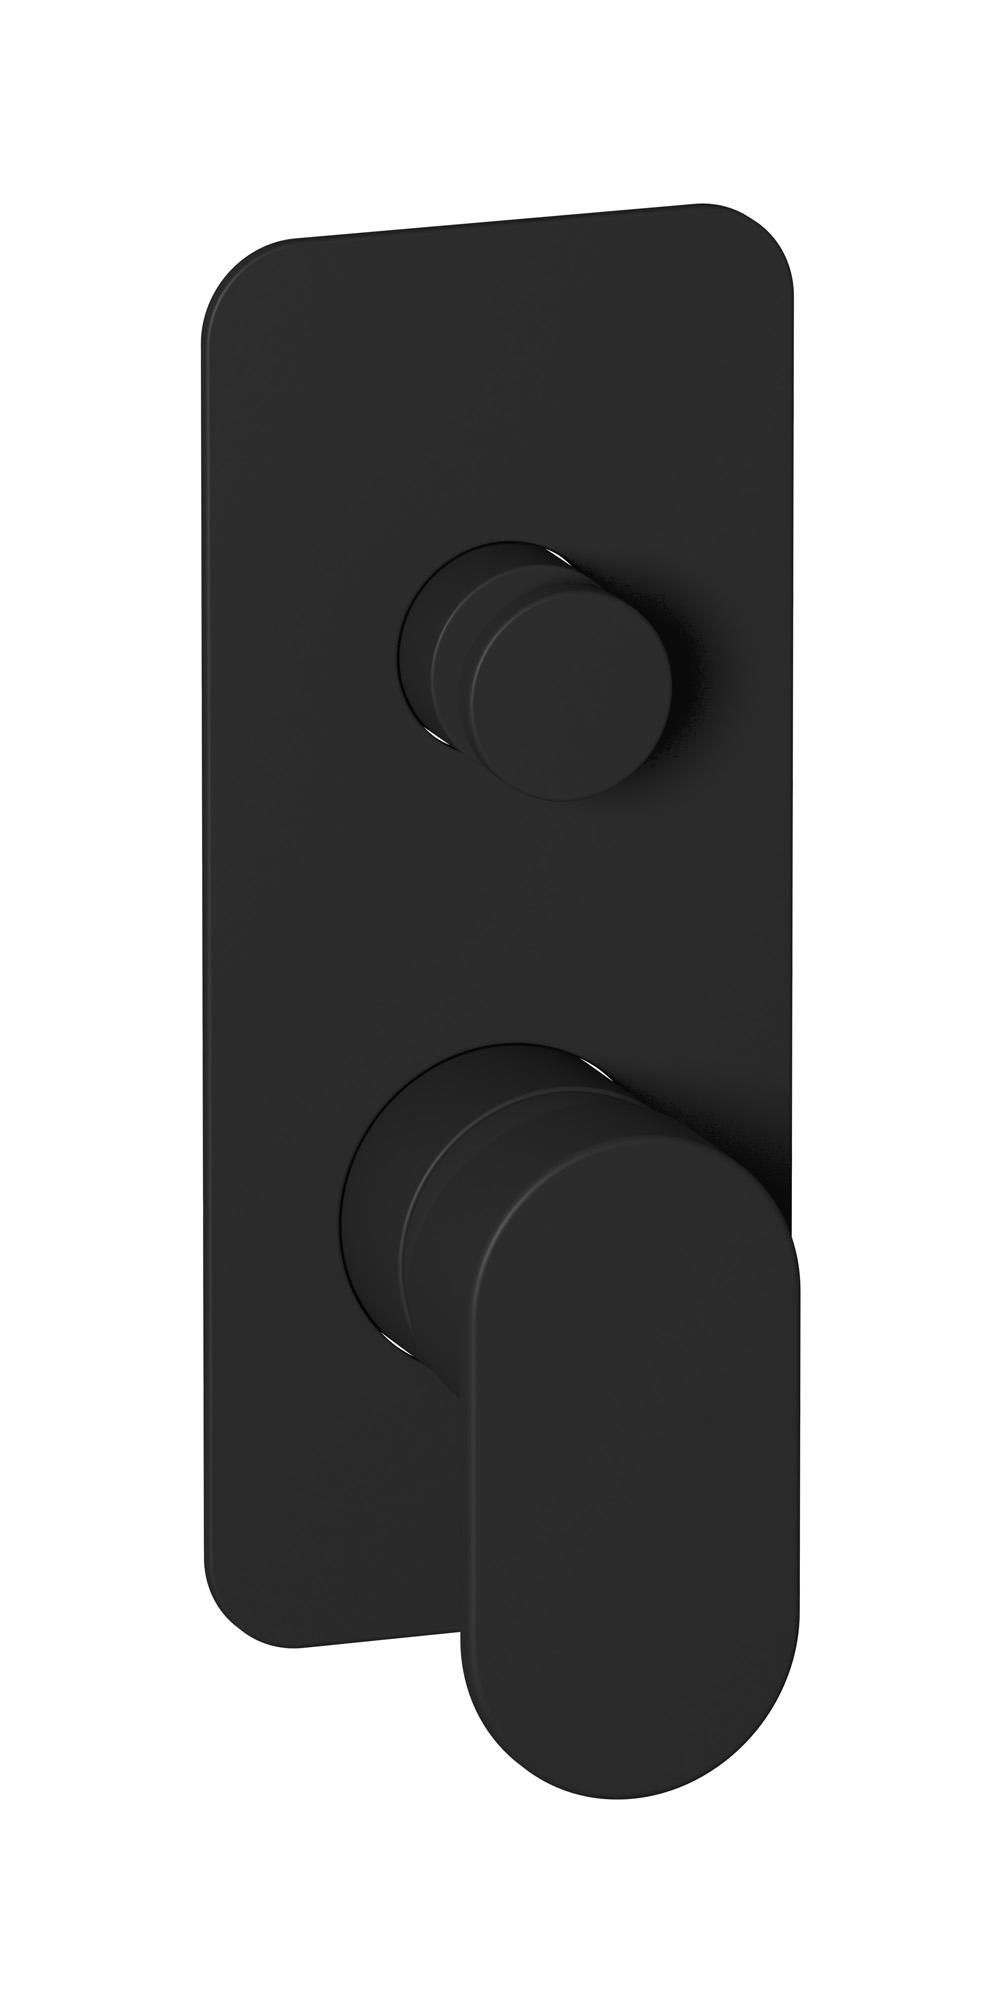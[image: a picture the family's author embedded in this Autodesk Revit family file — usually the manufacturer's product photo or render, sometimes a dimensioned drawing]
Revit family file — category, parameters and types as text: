
# Revit family: LM310
name_source: partatom
category: Apparecchi idraulici
units: mm (PartAtom-declared; Revit-internal decimal feet)

## family parameters
Basato su piano di lavoro = No
Condiviso = No
Mantieni orientamento annotazione = No
Numero OmniClass = 23.45.55.17
Punto di calcolo locali = No
Quota connettore circolare = Usa diametro
Sempre verticale = Sì
Taglio con vuoti quando caricato = No
Tipo di parte = Normale
Titolo OmniClass = Mixing Faucets

## types (9) — shared parameters
Cold water inlet = 10 mm  [stored 0.0328084 ft]
Commenti sul tipo = Wall mixer
Connessione CW = No
Connessione HW = No
Connessione di scarico = No
Connessione di ventilazione = No
Descrizione = Exposed parts for manual wall mixer with two ways diverter
Hot water inlet = 10 mm  [stored 0.0328084 ft]
Produttore = IB Rubinetterie S.p.A.
URL = https://www.weareib.it
zero-valued in all types: Prospetto di default

## per-type parameters (varying)
| type | Finishes surface | Immagine tipo | Modello |
| Chrome | IB_Chrome | LM310CC.jpg | LM310CC |
| Brushed nickel | IB_Brushed nickel | LM310SS.jpg | LM310SS |
| Natural brass | IB_Brass | LM310ON.jpg | LM310ON |
| Matt white | IB_matt white | LM310BO.jpg | LM310BO |
| Matt black | IB_matt black | LM310NP.jpg | LM310NP |
| Brushed black chrome | IB_Brushed black chrome | LM310CS.jpg | LM310CS |
| Brushed rose gold | IB_Brushed rose gold | LM310SR.jpg | LM310SR |
| Brushed gold | IB_brushed gold | LM310OS.jpg | LM310OS |
| Brushed pale gold | IB_brushed pale gold | LM310IS.jpg | LM310IS |

note: [stored X ft] marks values corroborated as IEEE doubles in the binary element streams (Revit-internal decimal feet)
